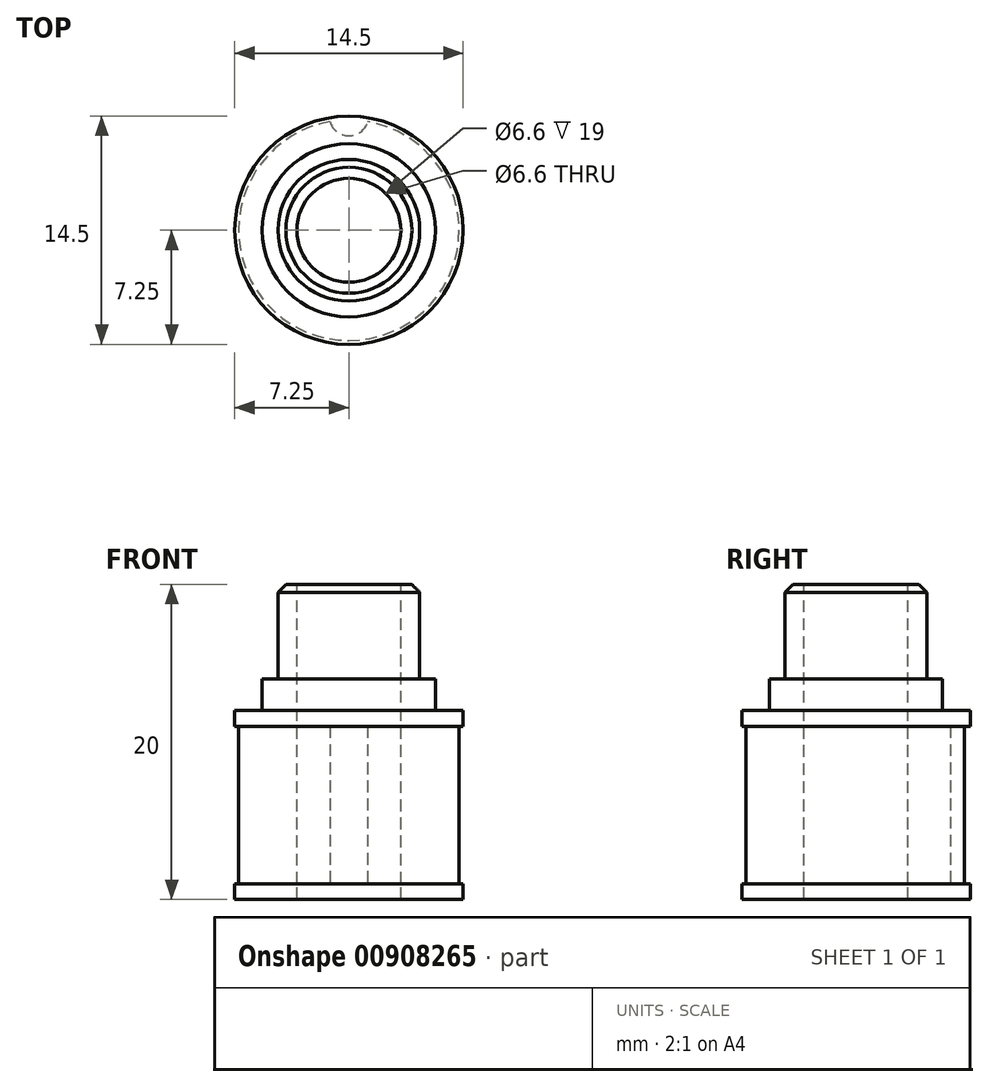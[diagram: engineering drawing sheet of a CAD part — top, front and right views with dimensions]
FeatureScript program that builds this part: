
annotation { "Feature Type Name" : "Feature", "Feature Type Description" : "" }
export const myFeature = defineFeature(function(context is Context, id is Id, definition is map)
    precondition{}
    {
        {
            var Q0;
            Q0=qCreatedBy(makeId("Top.planeOp"),FACE);
            var sketch = newSketch(context, id + "F0", { "sketchPlane" : qUnion([Q0])});
            skCircle(sketch, "E0", {"center": v(0, 0) * mm, "radius": 7.25 * mm});
            skSolve(sketch);
        }
        {
            var Q0;
            Q0=qSketchRegion(id+"F0",true);
            extrude(context, id + "F1", {"entities" : qUnion([Q0]), "depth" : 1 * mm, "offsetDistance" : 25 * mm});
        }
        {
            var Q0;
            Q0=makeQuery(id+"F1.opExtrude","CAP_FACE",FACE,{"disambiguationData":[OSD([sQuery(id+"F0.wireOp",EDGE,"E0")])],"isStart":false});
            var sketch = newSketch(context, id + "F2", { "sketchPlane" : qUnion([Q0])});
            skCircle(sketch, "E1", {"center": v(0, 0) * mm, "radius": 7.25 * mm});
            skSolve(sketch);
        }
        {
            var Q0;
            Q0=qSketchRegion(id+"F2",true);
            extrude(context, id + "F3", {"entities" : qUnion([Q0]), "depth" : 11 * mm, "offsetDistance" : 25 * mm});
        }
        {
            var Q0;
            Q0=makeQuery(id+"F3.opExtrude","CAP_FACE",FACE,{"disambiguationData":[OSD([sQuery(id+"F2.wireOp",EDGE,"E1")])],"isStart":true});
            var sketch = newSketch(context, id + "F4", { "sketchPlane" : qUnion([Q0])});
            skCircle(sketch, "E2", {"center": v(0, -7.25) * mm, "radius": 1.25 * mm});
            skSolve(sketch);
        }
        {
            var Q0;
            Q0=qSketchRegion(id+"F4",true);
            extrude(context, id + "F5", {"entities" : qUnion([Q0]), "operationType" : NewBodyOperationType.REMOVE, "oppositeDirection" : true, "depth" : 10 * mm, "offsetDistance" : 25 * mm});
        }
        {
            var Q0;
            Q0=makeQuery(id+"F3.opExtrude","CAP_FACE",FACE,{"disambiguationData":[OSD([sQuery(id+"F2.wireOp",EDGE,"E1")])],"isStart":true});
            var sketch = newSketch(context, id + "F6", { "sketchPlane" : qUnion([Q0])});
            skCircle(sketch, "E3", {"center": v(0, 0) * mm, "radius": 7.25 * mm});
            skCircle(sketch, "E4", {"center": v(0, 0) * mm, "radius": 7 * mm});
            skSolve(sketch);
        }
        {
            var Q0;
            Q0=qSketchRegion(id+"F6",true);
            extrude(context, id + "F7", {"entities" : qUnion([Q0]), "operationType" : NewBodyOperationType.REMOVE, "oppositeDirection" : true, "depth" : 10 * mm, "offsetDistance" : 25 * mm});
        }
        {
            var Q0;
            Q0=makeQuery(id+"F3.opExtrude","CAP_FACE",FACE,{"disambiguationData":[OSD([sQuery(id+"F2.wireOp",EDGE,"E1")])],"isStart":false});
            var sketch = newSketch(context, id + "F8", { "sketchPlane" : qUnion([Q0])});
            skCircle(sketch, "E5", {"center": v(0, 0) * mm, "radius": 5.5 * mm});
            skSolve(sketch);
        }
        {
            var Q0;
            Q0 = qSketchRegion(id + "F8", true);
            extrude(context, id + "F9", {"entities" : qUnion([Q0]), "operationType" : NewBodyOperationType.ADD, "depth" : 2 * mm, "offsetDistance" : 25 * mm});
        }
        {
            var Q0;
            Q0=makeQuery(id+"F9.opExtrude","CAP_FACE",FACE,{"disambiguationData":[OSD([sQuery(id+"F8.wireOp",EDGE,"E5")])],"isStart":false});
            var sketch = newSketch(context, id + "F10", { "sketchPlane" : qUnion([Q0])});
            skCircle(sketch, "E6", {"center": v(0, 0) * mm, "radius": 4.5 * mm});
            skSolve(sketch);
        }
        {
            var Q0;
            Q0 = qSketchRegion(id + "F10", true);
            extrude(context, id + "F11", {"entities" : qUnion([Q0]), "operationType" : NewBodyOperationType.ADD, "depth" : 6 * mm, "offsetDistance" : 25 * mm});
        }
        {
            var Q0;
            Q0=makeQuery(id+"F11.opExtrude","CAP_FACE",FACE,{"disambiguationData":[OSD([sQuery(id+"F10.wireOp",EDGE,"E6")])],"isStart":false});
            var sketch = newSketch(context, id + "F12", { "sketchPlane" : qUnion([Q0])});
            skCircle(sketch, "E7", {"center": v(0, 0) * mm, "radius": 3.3 * mm});
            skSolve(sketch);
        }
        {
            var Q0;
            Q0=makeQuery(id+"F12.imprint","IMPRINT",FACE,{"disambiguationData":[TD([[makeQuery(id+"F12.imprint","IMPRINT",EDGE,{"derivedFrom":sQuery(id+"F12.wireOp",EDGE,"E7")}),1.0]])]});
            extrude(context, id + "F13", {"entities" : qUnion([Q0]), "operationType" : NewBodyOperationType.REMOVE, "oppositeDirection" : true, "depth" : 25 * mm, "offsetDistance" : 25 * mm});
        }
        {
            var Q0;
            Q0=makeQuery(id+"F11.opExtrude","CAP_EDGE",EDGE,{"disambiguationData":[OSD([sQuery(id+"F10.wireOp",EDGE,"E6")])],"isStart":false});
            chamfer(context, id + "F14", {"entities" : qUnion([Q0]), "width" : 0.5 * mm, "tangentPropagation" : true});
        }
    });
